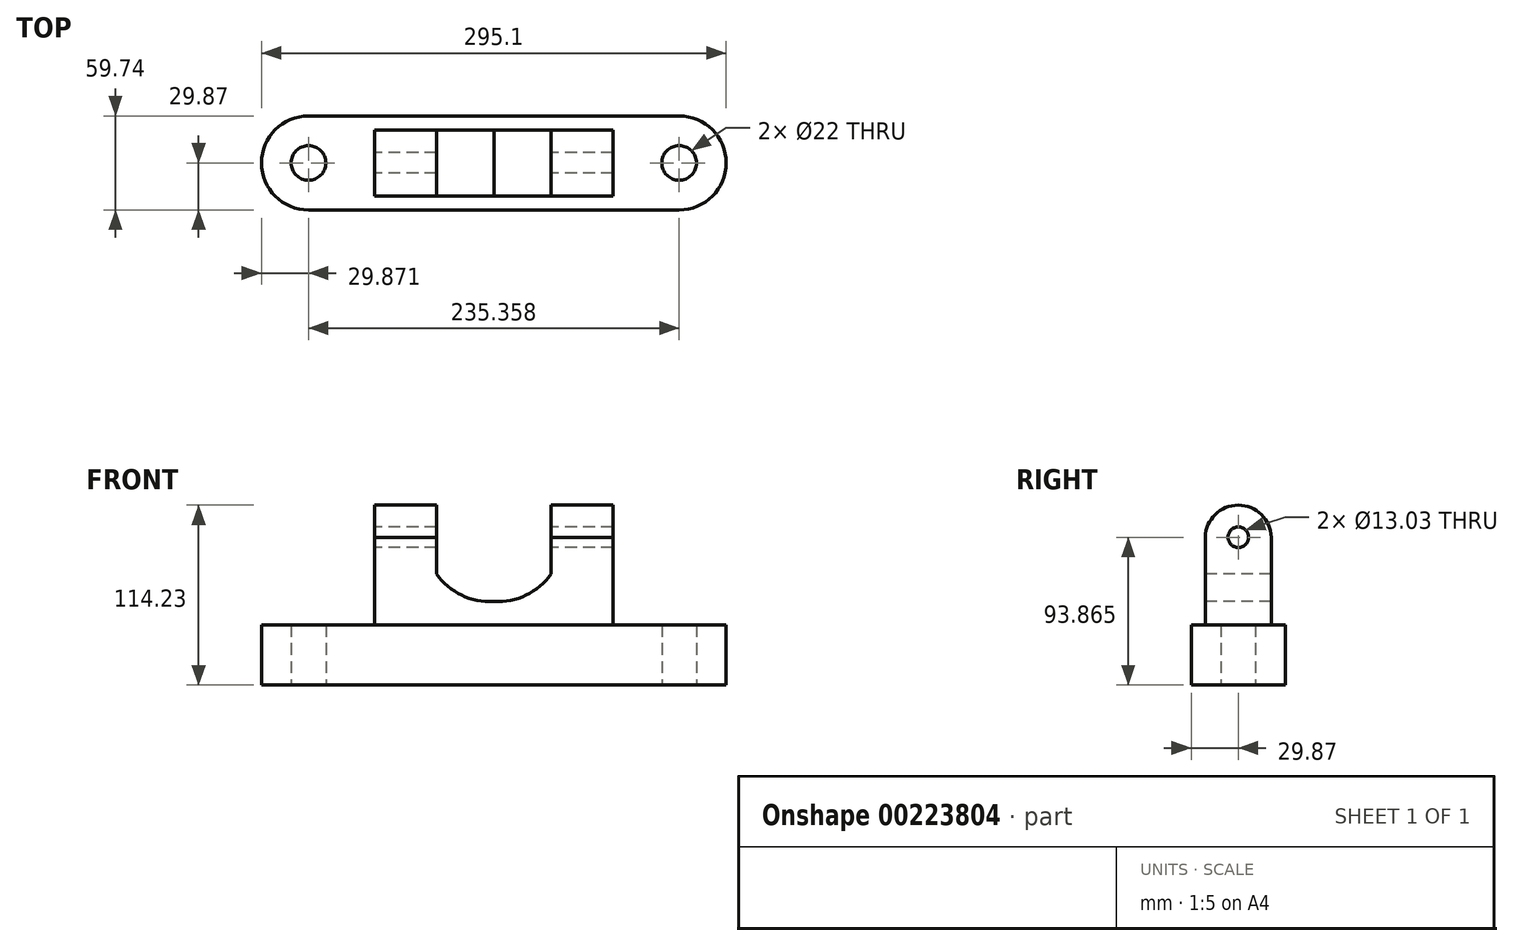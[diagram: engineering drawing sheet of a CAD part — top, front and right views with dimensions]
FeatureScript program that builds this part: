
annotation { "Feature Type Name" : "Feature", "Feature Type Description" : "" }
export const myFeature = defineFeature(function(context is Context, id is Id, definition is map)
    precondition{}
    {
        {
            var Q0;
            Q0=qCreatedBy(makeId("Top.planeOp"),FACE);
            var sketch = newSketch(context, id + "F0", { "sketchPlane" : qUnion([Q0])});
            skLineSegment(sketch, "E0.bottom", {"start": v(0, 29.87) * mm, "end": v(-117.68, 29.87) * mm});
            skLineSegment(sketch, "E0.top", {"start": v(0, -29.87) * mm, "end": v(-117.68, -29.87) * mm});
            skArc(sketch, "E1", {"start": v(-117.68, 29.87) * mm, "mid": v(-147.55, 0) * mm, "end": v(-117.68, -29.87) * mm});
            skLineSegment(sketch, "E2.MirrorCS", {"start": v(0, 29.87) * mm, "end": v(117.68, 29.87) * mm});
            skArc(sketch, "E3.MirrorCS", {"start": v(117.68, 29.87) * mm, "mid": v(147.55, 0) * mm, "end": v(117.68, -29.87) * mm});
            skLineSegment(sketch, "E4.MirrorCS", {"start": v(0, -29.87) * mm, "end": v(117.68, -29.87) * mm});
            skCircle(sketch, "E5", {"center": v(-117.68, 0) * mm, "radius": 11 * mm});
            skLineSegment(sketch, "E6", {"start": v(0, 29.87) * mm, "end": v(0, -29.87) * mm, "construction": true});
            skCircle(sketch, "E7.MirrorC", {"center": v(117.68, 0) * mm, "radius": 11 * mm});
            skSolve(sketch);
        }
        {
            var Q0;
            Q0 = qSketchRegion(id + "F0", true);
            extrude(context, id + "F1", {"entities" : qUnion([Q0]), "depth" : 38.1 * mm});
        }
        {
            var Q0;
            Q0=makeQuery(id+"F1.opExtrude","CAP_FACE",FACE,{"disambiguationData":[OSD([sQuery(id+"F0.wireOp",EDGE,"E0.bottom"),sQuery(id+"F0.wireOp",EDGE,"E0.top"),sQuery(id+"F0.wireOp",EDGE,"E1"),sQuery(id+"F0.wireOp",EDGE,"E2.MirrorCS"),sQuery(id+"F0.wireOp",EDGE,"E3.MirrorCS"),sQuery(id+"F0.wireOp",EDGE,"E4.MirrorCS"),sQuery(id+"F0.wireOp",EDGE,"E5"),sQuery(id+"F0.wireOp",EDGE,"E7.MirrorC")])],"isStart":false});
            var sketch = newSketch(context, id + "F2", { "sketchPlane" : qUnion([Q0])});
            skLineSegment(sketch, "E8", {"start": v(0, 29.87) * mm, "end": v(0, 20.94) * mm, "construction": true});
            skLineSegment(sketch, "E9.bottom", {"start": v(-75.7, 20.94) * mm, "end": v(0, 20.94) * mm});
            skLineSegment(sketch, "E9.top", {"start": v(-75.7, -20.94) * mm, "end": v(0, -20.94) * mm});
            skLineSegment(sketch, "E9.left", {"start": v(-75.7, 20.94) * mm, "end": v(-75.7, -20.94) * mm});
            skLineSegment(sketch, "E10.MirrorCS", {"start": v(75.7, 20.94) * mm, "end": v(0, 20.94) * mm});
            skLineSegment(sketch, "E11.MirrorCS", {"start": v(75.7, 20.94) * mm, "end": v(75.7, -20.94) * mm});
            skLineSegment(sketch, "E12.MirrorCS", {"start": v(75.7, -20.94) * mm, "end": v(0, -20.94) * mm});
            skLineSegment(sketch, "E13.trimOffspring", {"start": v(0, -20.94) * mm, "end": v(0, -29.87) * mm, "construction": true});
            skLineSegment(sketch, "E14", {"start": v(-75.7, 20.94) * mm, "end": v(75.7, -20.94) * mm, "construction": true});
            skLineSegment(sketch, "E15", {"start": v(-75.7, -20.94) * mm, "end": v(75.7, 20.94) * mm, "construction": true});
            skSolve(sketch);
        }
        {
            var Q0;
            Q0 = qSketchRegion(id + "F2", true);
            extrude(context, id + "F3", {"entities" : qUnion([Q0]), "operationType" : NewBodyOperationType.ADD, "depth" : 76.2 * mm});
        }
        {
            var Q0;
            Q0=makeQuery(id+"F3.opExtrude","SWEPT_FACE",FACE,{"disambiguationData":[OSD([sQuery(id+"F2.wireOp",EDGE,"E9.left")])]});
            var sketch = newSketch(context, id + "F4", { "sketchPlane" : qUnion([Q0])});
            skCircle(sketch, "E16", {"center": v(0, 93.86) * mm, "radius": 6.52 * mm});
            skLineSegment(sketch, "E17", {"start": v(0, 93.86) * mm, "end": v(-30.46, 93.86) * mm, "construction": true});
            skLineSegment(sketch, "E18", {"start": v(-30.46, 93.86) * mm, "end": v(27.4, 93.86) * mm, "construction": true});
            skArc(sketch, "E19", {"start": v(20.94, 93.86) * mm, "mid": v(0, 114.23) * mm, "end": v(-20.94, 93.86) * mm});
            skSolve(sketch);
        }
        {
            var Q0;
            Q0 = qSketchRegion(id + "F4", true);
            var Q1;
            {var subQ0=sQuery(id+"F4.wireOp",EDGE,"E19");Q1=makeQuery(id+"F4.imprint","IMPRINT",FACE,{"disambiguationData":[TD([[makeQuery(id+"F4.imprint","IMPRINT",EDGE,{"derivedFrom":subQ0}),-1.0]])]});}
            extrude(context, id + "F5", {"entities" : qUnion([Q0, Q1]), "operationType" : NewBodyOperationType.REMOVE, "endBound" : BoundingType.THROUGH_ALL, "oppositeDirection" : true, "depth" : 25.4 * mm});
        }
        {
            var Q0;
            Q0=makeQuery(id+"F3.opExtrude","SWEPT_FACE",FACE,{"disambiguationData":[OSD([sQuery(id+"F2.wireOp",EDGE,"E9.top"),sQuery(id+"F2.wireOp",EDGE,"E12.MirrorCS")])]});
            var sketch = newSketch(context, id + "F6", { "sketchPlane" : qUnion([Q0])});
            skLineSegment(sketch, "E20.0.2", {"start": v(36.44, 114.3) * mm, "end": v(-36.44, 114.3) * mm});
            skLineSegment(sketch, "E21", {"start": v(0, 38.1) * mm, "end": v(0, 114.3) * mm, "construction": true});
            skLineSegment(sketch, "E22", {"start": v(-36.44, 114.3) * mm, "end": v(-36.44, 70.6) * mm});
            skArc(sketch, "E23", {"start": v(-36.44, 70.6) * mm, "mid": v(-20.5, 57.08) * mm, "end": v(0, 53) * mm});
            skLineSegment(sketch, "E24.MirrorCS", {"start": v(36.44, 114.3) * mm, "end": v(36.44, 70.6) * mm});
            skArc(sketch, "E25.MirrorCS", {"start": v(36.44, 70.6) * mm, "mid": v(20.5, 57.08) * mm, "end": v(0, 53) * mm});
            skPoint(sketch, "E20.0.3.start.orphan", {"position": v(-75.97, 114.3) * mm});
            skPoint(sketch, "E20.0.0.start.orphan", {"position": v(-75.7, 38.1) * mm});
            skPoint(sketch, "E20.0.1.start.orphan", {"position": v(75.7, 38.1) * mm});
            skPoint(sketch, "E26.orphan", {"position": v(75.97, 114.3) * mm});
            skSolve(sketch);
        }
        {
            var Q0;
            Q0 = qSketchRegion(id + "F6", true);
            extrude(context, id + "F7", {"entities" : qUnion([Q0]), "operationType" : NewBodyOperationType.REMOVE, "endBound" : BoundingType.THROUGH_ALL, "oppositeDirection" : true, "depth" : 25.4 * mm});
        }
    });
